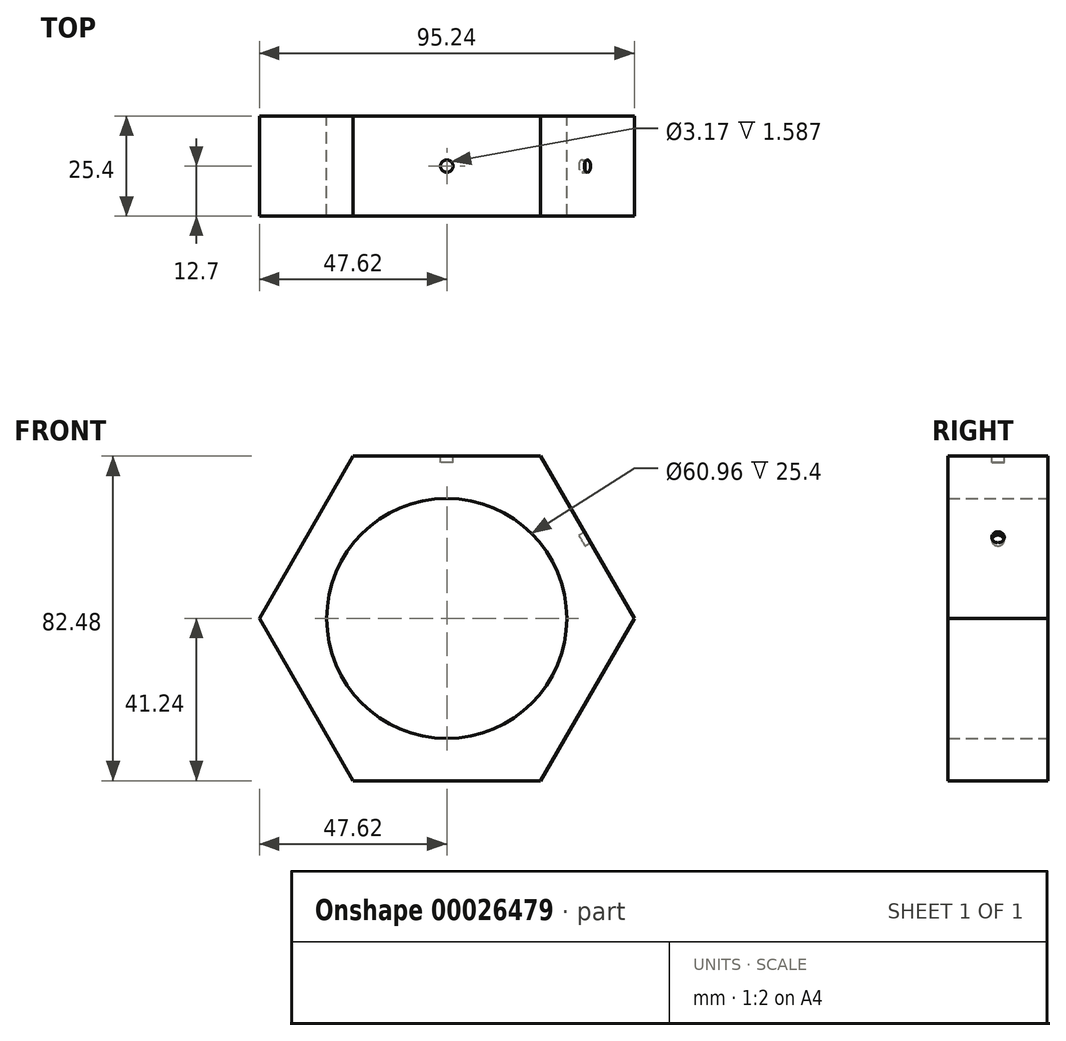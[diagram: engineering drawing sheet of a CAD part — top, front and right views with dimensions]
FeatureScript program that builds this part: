
annotation { "Feature Type Name" : "Feature", "Feature Type Description" : "" }
export const myFeature = defineFeature(function(context is Context, id is Id, definition is map)
    precondition{}
    {
        {
            var Q0;
            Q0=qCreatedBy(makeId("Front.planeOp"),FACE);
            var sketch = newSketch(context, id + "F0", { "sketchPlane" : qUnion([Q0])});
            skCircle(sketch, "E0", {"center": v(0, 0) * mm, "radius": 30.48 * mm});
            skCircle(sketch, "E1.cCircle", {"center": v(0, 0) * mm, "radius": 47.63 * mm, "construction": true});
            skLineSegment(sketch, "E1.0", {"start": v(-47.62, 0) * mm, "end": v(-23.81, 41.24) * mm});
            skLineSegment(sketch, "E1.1", {"start": v(-23.81, 41.24) * mm, "end": v(23.81, 41.24) * mm});
            skLineSegment(sketch, "E1.2", {"start": v(23.81, 41.24) * mm, "end": v(47.63, 0) * mm});
            skLineSegment(sketch, "E1.3", {"start": v(47.63, 0) * mm, "end": v(23.81, -41.24) * mm});
            skLineSegment(sketch, "E1.4", {"start": v(23.81, -41.24) * mm, "end": v(-23.81, -41.24) * mm});
            skLineSegment(sketch, "E1.5", {"start": v(-23.81, -41.24) * mm, "end": v(-47.63, 0) * mm});
            skSolve(sketch);
        }
        {
            var Q0;
            Q0 = qSketchRegion(id + "F0", true);
            extrude(context, id + "F1", {"entities" : qUnion([Q0]), "endBound" : BoundingType.SYMMETRIC, "depth" : 25.4 * mm});
        }
        {
            var Q0;
            Q0=makeQuery(id+"F1.opExtrude","SWEPT_FACE",FACE,{"disambiguationData":[OSD([sQuery(id+"F0.wireOp",EDGE,"E1.2")])]});
            var sketch = newSketch(context, id + "F2", { "sketchPlane" : qUnion([Q0])});
            skCircle(sketch, "E2", {"center": v(0, 0) * mm, "radius": 1.59 * mm});
            skPoint(sketch, "E2.centerSnap0", {"position": v(0, -23.81) * mm});
            skSolve(sketch);
        }
        {
            var Q0;
            Q0=makeQuery(id+"F2.imprint","IMPRINT",FACE,{"disambiguationData":[TD([[makeQuery(id+"F2.imprint","IMPRINT",EDGE,{"derivedFrom":sQuery(id+"F2.wireOp",EDGE,"E2")}),1.0]])]});
            extrude(context, id + "F3", {"entities" : qUnion([Q0]), "operationType" : NewBodyOperationType.REMOVE, "oppositeDirection" : true, "depth" : 1.59 * mm});
        }
        {
            var Q0;
            Q0=makeQuery(id+"F1.opExtrude","SWEPT_FACE",FACE,{"disambiguationData":[OSD([sQuery(id+"F0.wireOp",EDGE,"E1.1")])]});
            var sketch = newSketch(context, id + "F4", { "sketchPlane" : qUnion([Q0])});
            skCircle(sketch, "E3", {"center": v(0, 0) * mm, "radius": 1.59 * mm});
            skSolve(sketch);
        }
        {
            var Q0;
            Q0=makeQuery(id+"F4.imprint","IMPRINT",FACE,{"disambiguationData":[TD([[makeQuery(id+"F4.imprint","IMPRINT",EDGE,{"derivedFrom":sQuery(id+"F4.wireOp",EDGE,"E3")}),1.0]])]});
            extrude(context, id + "F5", {"entities" : qUnion([Q0]), "operationType" : NewBodyOperationType.REMOVE, "oppositeDirection" : true, "depth" : 1.59 * mm});
        }
    });
